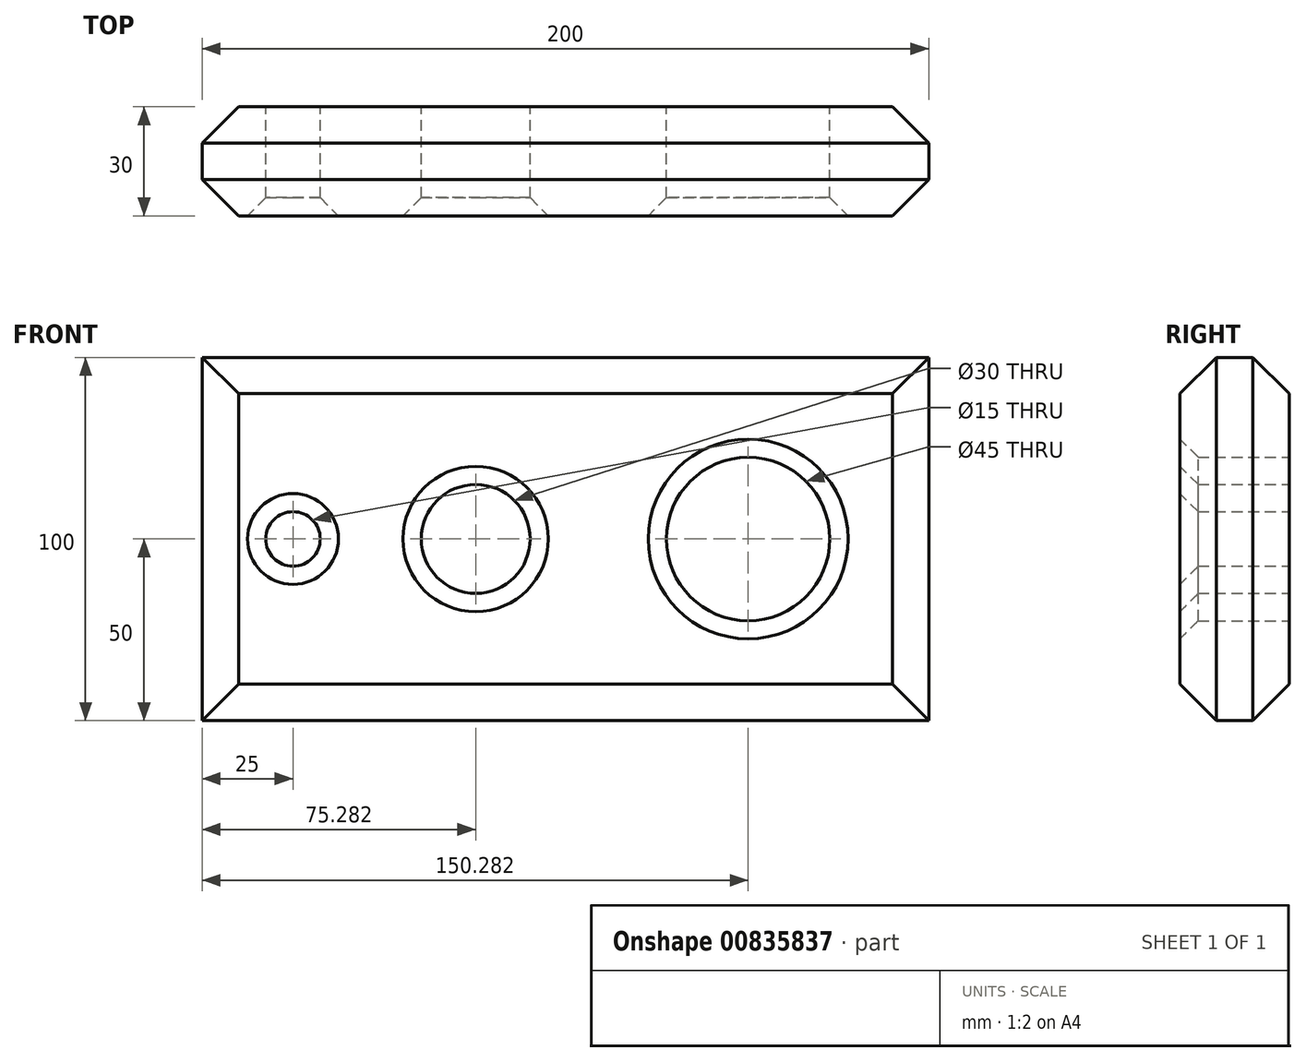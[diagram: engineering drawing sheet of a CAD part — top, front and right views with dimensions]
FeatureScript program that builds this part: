
annotation { "Feature Type Name" : "Feature", "Feature Type Description" : "" }
export const myFeature = defineFeature(function(context is Context, id is Id, definition is map)
    precondition{}
    {
        {
            var Q0;
            Q0=qCreatedBy(makeId("Front.planeOp"),FACE);
            var sketch = newSketch(context, id + "F0", { "sketchPlane" : qUnion([Q0])});
            skLineSegment(sketch, "E0.bottom", {"start": v(100, 50) * mm, "end": v(-100, 50) * mm});
            skLineSegment(sketch, "E0.top", {"start": v(100, -50) * mm, "end": v(-100, -50) * mm});
            skLineSegment(sketch, "E0.left", {"start": v(100, 50) * mm, "end": v(100, -50) * mm});
            skLineSegment(sketch, "E0.right", {"start": v(-100, 50) * mm, "end": v(-100, -50) * mm});
            skPoint(sketch, "E0.middle", {"position": v(0, 0) * mm});
            skCircle(sketch, "E1", {"center": v(-75, 0) * mm, "radius": 7.5 * mm});
            skCircle(sketch, "E2", {"center": v(-24.72, 0) * mm, "radius": 15 * mm});
            skCircle(sketch, "E3", {"center": v(50.28, 0) * mm, "radius": 22.5 * mm});
            skSolve(sketch);
        }
        {
            var Q0;
            Q0=makeQuery(id+"F0.imprint","IMPRINT",FACE,{"disambiguationData":[TD([[makeQuery(id+"F0.imprint","IMPRINT",EDGE,{"derivedFrom":sQuery(id+"F0.wireOp",EDGE,"E0.bottom")}),1.0]])]});
            extrude(context, id + "F1", {"entities" : qUnion([Q0]), "depth" : 30 * mm, "offsetDistance" : 25 * mm});
        }
        {
            var Q0;
            Q0=makeQuery(id+"F1.opExtrude","CAP_EDGE",EDGE,{"disambiguationData":[OSD([sQuery(id+"F0.wireOp",EDGE,"E2")])],"isStart":false});
            var Q1;
            Q1=makeQuery(id+"F1.opExtrude","CAP_EDGE",EDGE,{"disambiguationData":[OSD([sQuery(id+"F0.wireOp",EDGE,"E1")])],"isStart":false});
            var Q2;
            Q2=makeQuery(id+"F1.opExtrude","CAP_EDGE",EDGE,{"disambiguationData":[OSD([sQuery(id+"F0.wireOp",EDGE,"E3")])],"isStart":false});
            chamfer(context, id + "F2", {"entities" : qUnion([Q0, Q1, Q2]), "chamferType" : ChamferType.OFFSET_ANGLE, "width" : 5 * mm, "oppositeDirection" : false, "angle" : 45 * degree, "tangentPropagation" : true});
        }
        {
            var Q0;
            Q0=makeQuery(id+"F1.opExtrude","CAP_EDGE",EDGE,{"disambiguationData":[OSD([sQuery(id+"F0.wireOp",EDGE,"E0.bottom")])],"isStart":false});
            var Q1;
            Q1=makeQuery(id+"F1.opExtrude","CAP_EDGE",EDGE,{"disambiguationData":[OSD([sQuery(id+"F0.wireOp",EDGE,"E0.right")])],"isStart":false});
            var Q2;
            Q2=makeQuery(id+"F1.opExtrude","CAP_EDGE",EDGE,{"disambiguationData":[OSD([sQuery(id+"F0.wireOp",EDGE,"E0.top")])],"isStart":false});
            var Q3;
            Q3=makeQuery(id+"F1.opExtrude","CAP_EDGE",EDGE,{"disambiguationData":[OSD([sQuery(id+"F0.wireOp",EDGE,"E0.left")])],"isStart":false});
            var Q4;
            Q4=makeQuery(id+"F1.opExtrude","CAP_EDGE",EDGE,{"disambiguationData":[OSD([sQuery(id+"F0.wireOp",EDGE,"E0.left")])],"isStart":true});
            var Q5;
            Q5=makeQuery(id+"F1.opExtrude","CAP_EDGE",EDGE,{"disambiguationData":[OSD([sQuery(id+"F0.wireOp",EDGE,"E0.bottom")])],"isStart":true});
            var Q6;
            Q6=makeQuery(id+"F1.opExtrude","CAP_EDGE",EDGE,{"disambiguationData":[OSD([sQuery(id+"F0.wireOp",EDGE,"E0.top")])],"isStart":true});
            var Q7;
            Q7=makeQuery(id+"F1.opExtrude","CAP_EDGE",EDGE,{"disambiguationData":[OSD([sQuery(id+"F0.wireOp",EDGE,"E0.right")])],"isStart":true});
            chamfer(context, id + "F3", {"entities" : qUnion([Q0, Q1, Q2, Q3, Q4, Q5, Q6, Q7]), "chamferType" : ChamferType.OFFSET_ANGLE, "width" : 10 * mm, "oppositeDirection" : false, "angle" : 45 * degree, "tangentPropagation" : true});
        }
    });
